# Revit family: Sanitary_Shower-trays_Ideal-Standard_ULTRAFLT-S-S-TRAY_k8320
name_source: partatom
category: Plumbing Fixtures
revit_build: Autodesk Revit 2017 (Build: 20160225_1515(x64)
units: mm (PartAtom-declared; Revit-internal decimal feet)

## family parameters
Always vertical = No
Cut with Voids When Loaded = No
OmniClass Number = 23.45.05.14.21
OmniClass Title = Bathtubs
Part Type = Normal
Room Calculation Point = No
Round Connector Dimension = Use Diameter
Shared = No
Work Plane-Based = No

## types (6) — shared parameters
BIMobject category = Shower trays
BIMobject category code = sanitary-shower-trays
BIMobject main category = Sanitary
BIMobject main category code = sanitary
BOSUseNativeGeometries = 1
Brand url = http://www.idealstandard.it
Date of publishing = 2019_01_04
Edition number = 1
IFC Classification = IfcSanitaryTerminal
Installation instructions = http://www.idealstandard.it
Manufacturer name = Ideal Standard
Material main = IdelaSolid
NBS Reference Code = Pr_40_20_06_84
NBS Reference Description = Shower Trays
OmniClass Code = 23-31 17 00
OmniClass Description = Showers
Product Guid = 6f2a706b-9e76-46e7-a264-a3b575d17078
Product SKU = K8320
Product certification = http://www.idealstandard.it
Product data url = https://bimobject.com
Product family = Sanitary
Product group = Shower trays
Product name = ULTRAFLT S S/TRAY 180X100 BC SAND RECT
Product url = http://www.idealstandard.it
QR code = http://bimobject.com
Technical description = http://www.idealstandard.it
URL = http://www.idealstandard.it
Uniclass 1.4 Code = L72143
Uniclass 1.4 Description = Shower trays
Uniclass 2.0 Code = PR-35-06-84
Uniclass 2.0 Description = Shower Trays
Uniclass 2015 Code = SL_35_80_80
Uniclass 2015 Name = Showers
Youtube clip = https://www.youtube.com

## per-type parameters (varying)
| type | EAN code | Model |
| K8320DD - ULTRAFLT S S/TRAY 180X100 RECT STD CUT | https://4015413077828 | K8320DD |
| K8320FR - ULTRAFLT S S/TRAY 180X100 PURE WH RECT | https://4015413077736 | K8320FR |
| K8320FS - ULTRAFLT S S/TRAY 180X100 CONC GR RECT | https://4015413077750 | K8320FS |
| K8320FT - ULTRAFLT S S/TRAY 180X100 BC SAND RECT | https://4015413077767 | K8320FT |
| K8320FU - ULTRAFLT S S/TRAY 180X100 DP MOKA RECT | https://4015413077774 | K8320FU |
| K8320FV - ULTRAFLT S S/TRAY 180X100 JET BLK RECT | https://4015413077804 | K8320FV |

## geometry (parser evidence)
native form markers: Sweep x2
no freeform markers — native parametric forms only
